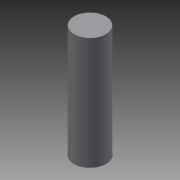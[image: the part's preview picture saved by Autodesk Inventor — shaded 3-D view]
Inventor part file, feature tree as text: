
AUTODESK INVENTOR PART (.ipt)
format: ipt  version: 2015 (Build 190159000, 159)  size: 67,072 bytes
history: native  units: mm
features: extrude x1, sketch x1
ambient origin geometry x8: Origin, YZ Plane, XZ Plane, XY Plane, X Axis, Y Axis, Z Axis, Center Point
bodies: Solid1 (feature_tree)
feature tree (2):
  extrude  "Extrusion1"  Depth=65.3mm TaperAngle=0.0deg
  sketch  "Sketch1"  dims[d0=18.5mm d1=65.3mm d2=0.0mm]
